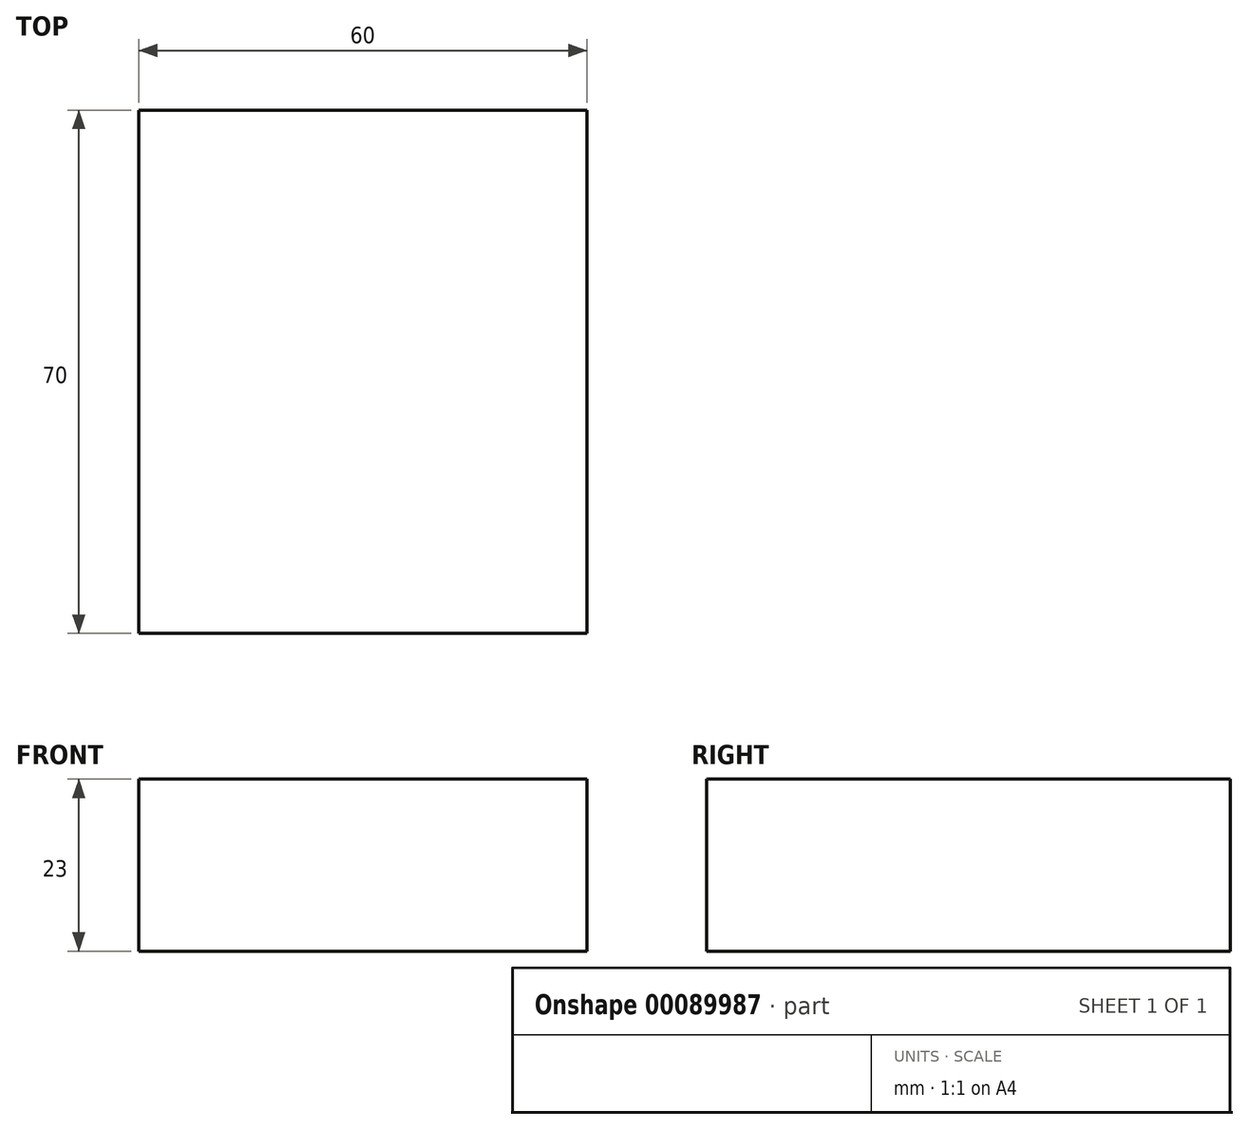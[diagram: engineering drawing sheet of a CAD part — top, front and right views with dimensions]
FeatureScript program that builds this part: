
annotation { "Feature Type Name" : "Feature", "Feature Type Description" : "" }
export const myFeature = defineFeature(function(context is Context, id is Id, definition is map)
    precondition{}
    {
        {
            var Q0;
            Q0=qCreatedBy(makeId("Top.planeOp"),FACE);
            var sketch = newSketch(context, id + "F0", { "sketchPlane" : qUnion([Q0])});
            skLineSegment(sketch, "E0.bottom", {"start": v(0, 0) * mm, "end": v(60, 0) * mm});
            skLineSegment(sketch, "E0.top", {"start": v(0, 70) * mm, "end": v(60, 70) * mm});
            skLineSegment(sketch, "E0.left", {"start": v(0, 0) * mm, "end": v(0, 70) * mm});
            skLineSegment(sketch, "E0.right", {"start": v(60, 0) * mm, "end": v(60, 70) * mm});
            skSolve(sketch);
        }
        {
            var Q0;
            Q0 = qSketchRegion(id + "F0", true);
            extrude(context, id + "F1", {"entities" : qUnion([Q0]), "depth" : 23 * mm});
        }
    });
